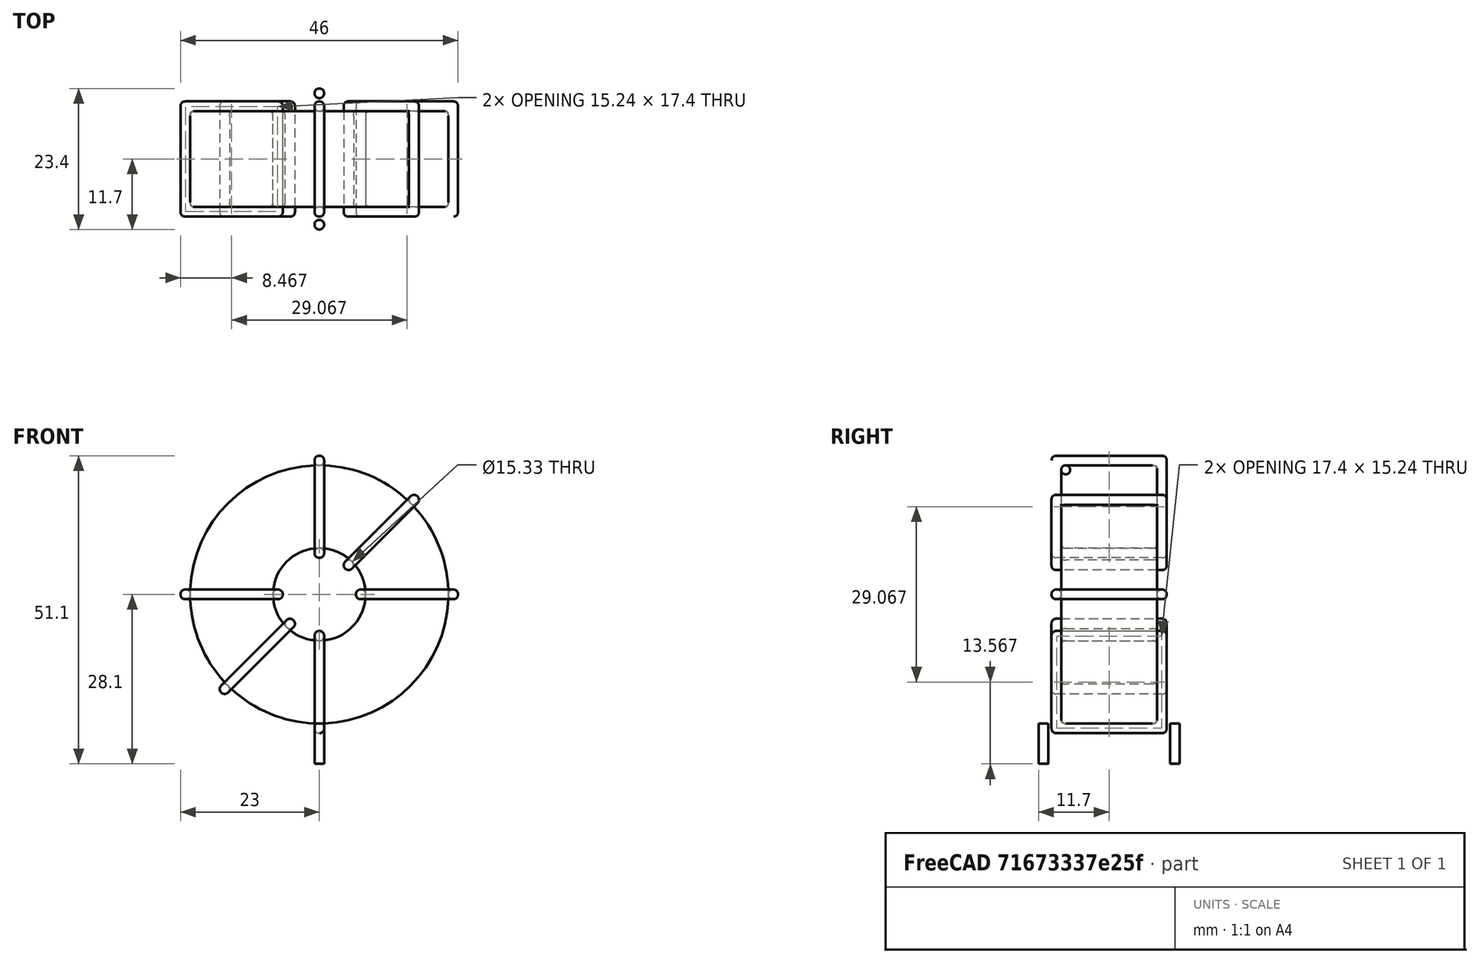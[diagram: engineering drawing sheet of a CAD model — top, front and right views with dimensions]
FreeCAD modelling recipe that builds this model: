
FCSTD DOCUMENT  (FreeCAD 0.16R6703 (Git))
Label: L_Toroid_Vertical_L46.0mm_W19.1mm_P21.80mm_Bourns_5700series
License: All rights reserved
LicenseURL: http://en.wikipedia.org/wiki/All_rights_reserved
objects: Sketcher::SketchObject×6, PartDesign::Pad×6, PartDesign::Fillet×5, Spreadsheet::Sheet×1
note: 23 computed .brp shape members not serialized (recipe doc carries the construction recipe); baked Part::Feature solids carry a one-line shape summary decoded from their .brp

FEATURE [Spreadsheet::Sheet] Spreadsheet  label="dimensions"
  cells = A1=Wx; B1(Wx)=46; C1(WW)=15.33333333333333; D1=46; A2=Wy; B2(Wy)=19.1; D2=19.1; A3=RM; B3(RMx)=21.8; C3(RMy)=0; A4=d_wire; B4(d_wire)=1.6; A5=H; B5(H)=46; A6=offsetx; B6(offsetx)=23
FEATURE [Sketcher::SketchObject] Sketch
  Placement = pos=(0,-10.9,0) rot=(1,0,0;1.5708rad)
  expr: Placement.Base.y = -Spreadsheet.RMx / 2
  expr: Constraints[0] = Spreadsheet.Wx / 2 - Spreadsheet.d_wire
  expr: Constraints[4] = Spreadsheet.WW / 2
  expr: Constraints[2] = Spreadsheet.Wx / 2 + Spreadsheet.d_wire + 0.5
  sketch-geometry (2):
    g0: Circle CenterX=0 CenterY=25.1 CenterZ=0 NormalX=0 NormalY=0 NormalZ=1 Radius=21.4
    g1: Circle CenterX=0 CenterY=25.1 CenterZ=0 NormalX=0 NormalY=0 NormalZ=1 Radius=7.66667
  constraints (5):
    c: Radius(g0) = 21.4
    c: DistanceX(g-1,g0) = 0
    c: DistanceY(g-1,g0) = 25.1
    c: Coincident(g1,g0)
    c: Radius(g1) = 7.66667
FEATURE [PartDesign::Pad] Pad
  Length = 15.9
  Length2 = 100
  Midplane = true
  Placement = pos=(0,-10.9,0) rot=(1,0,0;1.5708rad)
  Sketch = -> Sketch
  Type = 0
  expr: Length = Spreadsheet.Wy - 2 * Spreadsheet.d_wire
FEATURE [Sketcher::SketchObject] Sketch001
  Placement = pos=(0,0,2.1) rot=(0,0,1;0rad)
  expr: Placement.Base.z = 0.5 + Spreadsheet.d_wire
  expr: Constraints[4] = Spreadsheet.RMy
  expr: Constraints[2] = -Spreadsheet.RMx
  expr: Constraints[1] = Spreadsheet.d_wire / 2
  sketch-geometry (2):
    g0: Circle CenterX=0 CenterY=0 CenterZ=0 NormalX=0 NormalY=0 NormalZ=1 Radius=0.8
    g1: Circle CenterX=0 CenterY=-21.8 CenterZ=0 NormalX=0 NormalY=0 NormalZ=1 Radius=0.8
  constraints (5):
    c: Equal(g0,g1)
    c: Radius(g0) = 0.8
    c: DistanceY(g-1,g1) = -21.8
    c: Coincident(g0,g-1)
    c: DistanceX(g-1,g1) = 0
FEATURE [PartDesign::Pad] Pad001
  Length = 1.6
  Length2 = 5.1
  Placement = pos=(0,0,2.1) rot=(0,0,1;0rad)
  Reversed = true
  Sketch = -> Sketch001
  Type = 4
  expr: Length2 = 3.5 + Spreadsheet.d_wire
  expr: Length = Spreadsheet.d_wire
FEATURE [PartDesign::Fillet] Fillet
  Base = -> Pad [Edge6,Edge3,Edge2]
  Placement = pos=(0,-10.9,0) rot=(1,0,0;1.5708rad)
  Radius = 0.5
FEATURE [Sketcher::SketchObject] Sketch003
  Placement = pos=(0,-1.35,25.1) rot=(1,0,0;3.14159rad)
  expr: Constraints[18] = Spreadsheet.d_wire
  expr: Constraints[16] = Spreadsheet.d_wire
  expr: Constraints[19] = Spreadsheet.d_wire
  expr: Constraints[17] = Spreadsheet.d_wire
  expr: Placement.Base.y = -1 * (Spreadsheet.RMx - Spreadsheet.Wy) / 2
  expr: Constraints[21] = (Spreadsheet.Wx - Spreadsheet.WW) / 2 - Spreadsheet.d_wire
  expr: Constraints[22] = Spreadsheet.Wx / 2 - Spreadsheet.d_wire
  expr: Constraints[43] = Spreadsheet.d_wire
  expr: Constraints[48] = Spreadsheet.Wx - Spreadsheet.d_wire * 2
  expr: Constraints[49] = Spreadsheet.Wy
  expr: Placement.Base.z = Spreadsheet.Wx / 2 + Spreadsheet.d_wire + 0.5
  sketch-geometry (16):
    g0: LineSegment StartX=-6.06667 StartY=0 StartZ=0 EndX=-23 EndY=0 EndZ=0
    g1: LineSegment StartX=-23 StartY=0 StartZ=0 EndX=-23 EndY=19.1 EndZ=0
    g2: LineSegment StartX=-23 StartY=19.1 StartZ=0 EndX=-6.06667 EndY=19.1 EndZ=0
    g3: LineSegment StartX=-6.06667 StartY=19.1 StartZ=0 EndX=-6.06667 EndY=0 EndZ=0
    g4: LineSegment StartX=-21.4 StartY=17.5 StartZ=0 EndX=-7.66667 EndY=17.5 EndZ=0
    g5: LineSegment StartX=-7.66667 StartY=17.5 StartZ=0 EndX=-7.66667 EndY=1.6 EndZ=0
    g6: LineSegment StartX=-7.66667 StartY=1.6 StartZ=0 EndX=-21.4 EndY=1.6 EndZ=0
    g7: LineSegment StartX=-21.4 StartY=1.6 StartZ=0 EndX=-21.4 EndY=17.5 EndZ=0
    g8: LineSegment StartX=6.06667 StartY=19.1 StartZ=0 EndX=23 EndY=19.1 EndZ=0
    g9: LineSegment StartX=23 StartY=19.1 StartZ=0 EndX=23 EndY=0 EndZ=0
    g10: LineSegment StartX=23 StartY=0 StartZ=0 EndX=6.06667 EndY=0 EndZ=0
    g11: LineSegment StartX=6.06667 StartY=0 StartZ=0 EndX=6.06667 EndY=19.1 EndZ=0
    g12: LineSegment StartX=7.66667 StartY=17.5 StartZ=0 EndX=21.4 EndY=17.5 EndZ=0
    g13: LineSegment StartX=21.4 StartY=17.5 StartZ=0 EndX=21.4 EndY=1.6 EndZ=0
    g14: LineSegment StartX=21.4 StartY=1.6 StartZ=0 EndX=7.66667 EndY=1.6 EndZ=0
    g15: LineSegment StartX=7.66667 StartY=1.6 StartZ=0 EndX=7.66667 EndY=17.5 EndZ=0
  constraints (50):
    c: Horizontal(g0)
    c: Coincident(g1,g0)
    c: Vertical(g1)
    c: Coincident(g2,g1)
    c: Horizontal(g2)
    c: Coincident(g3,g2)
    c: Coincident(g3,g0)
    c: Vertical(g3)
    c: Coincident(g4,g5)
    c: Coincident(g5,g6)
    c: Coincident(g6,g7)
    c: Coincident(g7,g4)
    c: Horizontal(g4)
    c: Horizontal(g6)
    c: Vertical(g5)
    c: Vertical(g7)
    c: DistanceX(g1,g4) = 1.6
    c: DistanceY(g4,g1) = 1.6
    c: DistanceX(g5,g0) = 1.6
    c: DistanceY(g0,g5) = 1.6
    c: DistanceY(g-1,g0) = 0
    c: DistanceX(g6,g6) = 13.7333
    c: DistanceX(g6,g-1) = 21.4
    c: Coincident(g8,g9)
    c: Coincident(g9,g10)
    c: Coincident(g10,g11)
    c: Coincident(g11,g8)
    c: Horizontal(g8)
    c: Horizontal(g10)
    c: Vertical(g9)
    c: Vertical(g11)
    c: Coincident(g12,g13)
    c: Coincident(g13,g14)
    c: Coincident(g14,g15)
    c: Coincident(g15,g12)
    c: Horizontal(g12)
    c: Horizontal(g14)
    c: Vertical(g13)
    c: Vertical(g15)
    c: DistanceY(g8,g2) = 0
    c: DistanceY(g10,g0) = 0
    c: DistanceY(g14,g5) = 0
    c: DistanceY(g12,g4) = 0
    c: DistanceX(g8,g12) = 1.6
    c: Equal(g8,g2)
    c: Equal(g12,g4)
    c: Equal(g9,g1)
    c: Equal(g13,g7)
    c: DistanceX(g4,g12) = 42.8
    c: DistanceY(g0,g1) = 19.1
FEATURE [PartDesign::Pad] Pad002
  Length = 1.6
  Length2 = 100
  Midplane = true
  Placement = pos=(0,-1.35,25.1) rot=(1,0,0;3.14159rad)
  Sketch = -> Sketch003
  Type = 0
  expr: Length = Spreadsheet.d_wire
FEATURE [PartDesign::Fillet] Fillet001
  Base = -> Pad002 [Edge38,Edge41,Edge42,Edge43,Edge29,Edge32,Edge33,Edge34,Edge25,Edge35,Edge36,Edge13,Edge14,Edge15,Edge16,Edge17,Edge18,Edge19,Edge1,Edge2,Edge3,Edge4,Edge5,Edge6,Edge7,Edge37,Edge39,Edge40,Edge20,Edge23,Edge24,Edge21,Edge22,Edge8,Edge9,Edge10,Edge11,Edge12,Edge26,Edge27,+8 more]
  Placement = pos=(0,-1.35,25.1) rot=(1,0,0;3.14159rad)
  Radius = 0.752
  expr: Radius = Spreadsheet.d_wire * 0.47
FEATURE [Sketcher::SketchObject] Sketch004
  Placement = pos=(0,-1.35,25.1) rot=(0.92388,0,0.382683;3.14159rad)
  expr: Constraints[18] = Spreadsheet.d_wire
  expr: Constraints[16] = Spreadsheet.d_wire
  expr: Constraints[19] = Spreadsheet.d_wire
  expr: Constraints[17] = Spreadsheet.d_wire
  expr: Placement.Base.y = -1 * (Spreadsheet.RMx - Spreadsheet.Wy) / 2
  expr: Constraints[21] = (Spreadsheet.Wx - Spreadsheet.WW) / 2 - Spreadsheet.d_wire
  expr: Constraints[22] = Spreadsheet.Wx / 2 - Spreadsheet.d_wire
  expr: Constraints[43] = Spreadsheet.d_wire
  expr: Constraints[48] = Spreadsheet.Wx - 2 * Spreadsheet.d_wire
  expr: Constraints[49] = Spreadsheet.Wy
  expr: Placement.Base.z = Spreadsheet.Wx / 2 + Spreadsheet.d_wire + 0.5
  sketch-geometry (16):
    g0: LineSegment StartX=-6.06667 StartY=0 StartZ=0 EndX=-23 EndY=0 EndZ=0
    g1: LineSegment StartX=-23 StartY=0 StartZ=0 EndX=-23 EndY=19.1 EndZ=0
    g2: LineSegment StartX=-23 StartY=19.1 StartZ=0 EndX=-6.06667 EndY=19.1 EndZ=0
    g3: LineSegment StartX=-6.06667 StartY=19.1 StartZ=0 EndX=-6.06667 EndY=0 EndZ=0
    g4: LineSegment StartX=-21.4 StartY=17.5 StartZ=0 EndX=-7.66667 EndY=17.5 EndZ=0
    g5: LineSegment StartX=-7.66667 StartY=17.5 StartZ=0 EndX=-7.66667 EndY=1.6 EndZ=0
    g6: LineSegment StartX=-7.66667 StartY=1.6 StartZ=0 EndX=-21.4 EndY=1.6 EndZ=0
    g7: LineSegment StartX=-21.4 StartY=1.6 StartZ=0 EndX=-21.4 EndY=17.5 EndZ=0
    g8: LineSegment StartX=6.06667 StartY=19.1 StartZ=0 EndX=23 EndY=19.1 EndZ=0
    g9: LineSegment StartX=23 StartY=19.1 StartZ=0 EndX=23 EndY=0 EndZ=0
    g10: LineSegment StartX=23 StartY=0 StartZ=0 EndX=6.06667 EndY=0 EndZ=0
    g11: LineSegment StartX=6.06667 StartY=0 StartZ=0 EndX=6.06667 EndY=19.1 EndZ=0
    g12: LineSegment StartX=7.66667 StartY=17.5 StartZ=0 EndX=21.4 EndY=17.5 EndZ=0
    g13: LineSegment StartX=21.4 StartY=17.5 StartZ=0 EndX=21.4 EndY=1.6 EndZ=0
    g14: LineSegment StartX=21.4 StartY=1.6 StartZ=0 EndX=7.66667 EndY=1.6 EndZ=0
    g15: LineSegment StartX=7.66667 StartY=1.6 StartZ=0 EndX=7.66667 EndY=17.5 EndZ=0
  constraints (50):
    c: Horizontal(g0)
    c: Coincident(g1,g0)
    c: Vertical(g1)
    c: Coincident(g2,g1)
    c: Horizontal(g2)
    c: Coincident(g3,g2)
    c: Coincident(g3,g0)
    c: Vertical(g3)
    c: Coincident(g4,g5)
    c: Coincident(g5,g6)
    c: Coincident(g6,g7)
    c: Coincident(g7,g4)
    c: Horizontal(g4)
    c: Horizontal(g6)
    c: Vertical(g5)
    c: Vertical(g7)
    c: DistanceX(g1,g4) = 1.6
    c: DistanceY(g4,g1) = 1.6
    c: DistanceX(g5,g0) = 1.6
    c: DistanceY(g0,g5) = 1.6
    c: DistanceY(g-1,g0) = 0
    c: DistanceX(g6,g6) = 13.7333
    c: DistanceX(g6,g-1) = 21.4
    c: Coincident(g8,g9)
    c: Coincident(g9,g10)
    c: Coincident(g10,g11)
    c: Coincident(g11,g8)
    c: Horizontal(g8)
    c: Horizontal(g10)
    c: Vertical(g9)
    c: Vertical(g11)
    c: Coincident(g12,g13)
    c: Coincident(g13,g14)
    c: Coincident(g14,g15)
    c: Coincident(g15,g12)
    c: Horizontal(g12)
    c: Horizontal(g14)
    c: Vertical(g13)
    c: Vertical(g15)
    c: DistanceY(g8,g2) = 0
    c: DistanceY(g10,g0) = 0
    c: DistanceY(g14,g5) = 0
    c: DistanceY(g12,g4) = 0
    c: DistanceX(g8,g12) = 1.6
    c: Equal(g8,g2)
    c: Equal(g12,g4)
    c: Equal(g9,g1)
    c: Equal(g13,g7)
    c: DistanceX(g4,g12) = 42.8
    c: DistanceY(g0,g1) = 19.1
FEATURE [PartDesign::Pad] Pad003
  Length = 1.6
  Length2 = 100
  Midplane = true
  Placement = pos=(0,-1.35,25.1) rot=(0.92388,0,0.382683;3.14159rad)
  Sketch = -> Sketch004
  Type = 0
  expr: Length = Spreadsheet.d_wire
FEATURE [PartDesign::Fillet] Fillet002
  Base = -> Pad003 [Edge38,Edge41,Edge42,Edge43,Edge29,Edge32,Edge33,Edge34,Edge25,Edge35,Edge36,Edge13,Edge14,Edge15,Edge16,Edge17,Edge18,Edge19,Edge1,Edge2,Edge3,Edge4,Edge5,Edge6,Edge7,Edge37,Edge39,Edge40,Edge20,Edge23,Edge24,Edge21,Edge22,Edge8,Edge9,Edge10,Edge11,Edge12,Edge26,Edge27,+8 more]
  Placement = pos=(0,-1.35,25.1) rot=(0.92388,0,0.382683;3.14159rad)
  Radius = 0.752
  expr: Radius = Spreadsheet.d_wire * 0.47
FEATURE [Sketcher::SketchObject] Sketch005
  Placement = pos=(0,-1.35,25.1) rot=(0.92388,0,-0.382683;3.14159rad)
  expr: Constraints[18] = Spreadsheet.d_wire
  expr: Constraints[16] = Spreadsheet.d_wire
  expr: Constraints[19] = Spreadsheet.d_wire
  expr: Constraints[17] = Spreadsheet.d_wire
  expr: Placement.Base.y = -1 * (Spreadsheet.RMx - Spreadsheet.Wy) / 2
  expr: Constraints[21] = (Spreadsheet.Wx - Spreadsheet.WW) / 2 - Spreadsheet.d_wire
  expr: Constraints[22] = Spreadsheet.Wx / 2 - Spreadsheet.d_wire
  expr: Constraints[43] = Spreadsheet.d_wire
  expr: Constraints[48] = Spreadsheet.Wx - 2 * Spreadsheet.d_wire
  expr: Constraints[49] = Spreadsheet.Wy
  expr: Placement.Base.z = Spreadsheet.Wx / 2 + Spreadsheet.d_wire + 0.5
  sketch-geometry (16):
    g0: LineSegment StartX=-6.06667 StartY=0 StartZ=0 EndX=-23 EndY=0 EndZ=0
    g1: LineSegment StartX=-23 StartY=0 StartZ=0 EndX=-23 EndY=19.1 EndZ=0
    g2: LineSegment StartX=-23 StartY=19.1 StartZ=0 EndX=-6.06667 EndY=19.1 EndZ=0
    g3: LineSegment StartX=-6.06667 StartY=19.1 StartZ=0 EndX=-6.06667 EndY=0 EndZ=0
    g4: LineSegment StartX=-21.4 StartY=17.5 StartZ=0 EndX=-7.66667 EndY=17.5 EndZ=0
    g5: LineSegment StartX=-7.66667 StartY=17.5 StartZ=0 EndX=-7.66667 EndY=1.6 EndZ=0
    g6: LineSegment StartX=-7.66667 StartY=1.6 StartZ=0 EndX=-21.4 EndY=1.6 EndZ=0
    g7: LineSegment StartX=-21.4 StartY=1.6 StartZ=0 EndX=-21.4 EndY=17.5 EndZ=0
    g8: LineSegment StartX=6.06667 StartY=19.1 StartZ=0 EndX=23 EndY=19.1 EndZ=0
    g9: LineSegment StartX=23 StartY=19.1 StartZ=0 EndX=23 EndY=0 EndZ=0
    g10: LineSegment StartX=23 StartY=0 StartZ=0 EndX=6.06667 EndY=0 EndZ=0
    g11: LineSegment StartX=6.06667 StartY=0 StartZ=0 EndX=6.06667 EndY=19.1 EndZ=0
    g12: LineSegment StartX=7.66667 StartY=17.5 StartZ=0 EndX=21.4 EndY=17.5 EndZ=0
    g13: LineSegment StartX=21.4 StartY=17.5 StartZ=0 EndX=21.4 EndY=1.6 EndZ=0
    g14: LineSegment StartX=21.4 StartY=1.6 StartZ=0 EndX=7.66667 EndY=1.6 EndZ=0
    g15: LineSegment StartX=7.66667 StartY=1.6 StartZ=0 EndX=7.66667 EndY=17.5 EndZ=0
  constraints (50):
    c: Horizontal(g0)
    c: Coincident(g1,g0)
    c: Vertical(g1)
    c: Coincident(g2,g1)
    c: Horizontal(g2)
    c: Coincident(g3,g2)
    c: Coincident(g3,g0)
    c: Vertical(g3)
    c: Coincident(g4,g5)
    c: Coincident(g5,g6)
    c: Coincident(g6,g7)
    c: Coincident(g7,g4)
    c: Horizontal(g4)
    c: Horizontal(g6)
    c: Vertical(g5)
    c: Vertical(g7)
    c: DistanceX(g1,g4) = 1.6
    c: DistanceY(g4,g1) = 1.6
    c: DistanceX(g5,g0) = 1.6
    c: DistanceY(g0,g5) = 1.6
    c: DistanceY(g-1,g0) = 0
    c: DistanceX(g6,g6) = 13.7333
    c: DistanceX(g6,g-1) = 21.4
    c: Coincident(g8,g9)
    c: Coincident(g9,g10)
    c: Coincident(g10,g11)
    c: Coincident(g11,g8)
    c: Horizontal(g8)
    c: Horizontal(g10)
    c: Vertical(g9)
    c: Vertical(g11)
    c: Coincident(g12,g13)
    c: Coincident(g13,g14)
    c: Coincident(g14,g15)
    c: Coincident(g15,g12)
    c: Horizontal(g12)
    c: Horizontal(g14)
    c: Vertical(g13)
    c: Vertical(g15)
    c: DistanceY(g8,g2) = 0
    c: DistanceY(g10,g0) = 0
    c: DistanceY(g14,g5) = 0
    c: DistanceY(g12,g4) = 0
    c: DistanceX(g8,g12) = 1.6
    c: Equal(g8,g2)
    c: Equal(g12,g4)
    c: Equal(g9,g1)
    c: Equal(g13,g7)
    c: DistanceX(g4,g12) = 42.8
    c: DistanceY(g0,g1) = 19.1
FEATURE [PartDesign::Pad] Pad004
  Length = 1.6
  Length2 = 100
  Midplane = true
  Placement = pos=(0,-1.35,25.1) rot=(0.92388,0,-0.382683;3.14159rad)
  Sketch = -> Sketch005
  Type = 0
  expr: Length = Spreadsheet.d_wire
FEATURE [PartDesign::Fillet] Fillet003
  Base = -> Pad004 [Edge38,Edge41,Edge42,Edge43,Edge29,Edge32,Edge33,Edge34,Edge25,Edge35,Edge36,Edge13,Edge14,Edge15,Edge16,Edge17,Edge18,Edge19,Edge1,Edge2,Edge3,Edge4,Edge5,Edge6,Edge7,Edge37,Edge39,Edge40,Edge20,Edge23,Edge24,Edge21,Edge22,Edge8,Edge9,Edge10,Edge11,Edge12,Edge26,Edge27,+8 more]
  Placement = pos=(0,-1.35,25.1) rot=(0.92388,0,-0.382683;3.14159rad)
  Radius = 0.752
  expr: Radius = Spreadsheet.d_wire * 0.47
FEATURE [Sketcher::SketchObject] Sketch006
  Placement = pos=(0,-1.35,25.1) rot=(0.707107,0,0.707107;3.14159rad)
  expr: Constraints[18] = Spreadsheet.d_wire
  expr: Constraints[16] = Spreadsheet.d_wire
  expr: Constraints[19] = Spreadsheet.d_wire
  expr: Constraints[17] = Spreadsheet.d_wire
  expr: Placement.Base.y = -1 * (Spreadsheet.RMx - Spreadsheet.Wy) / 2
  expr: Constraints[21] = (Spreadsheet.Wx - Spreadsheet.WW) / 2 - Spreadsheet.d_wire
  expr: Constraints[22] = Spreadsheet.Wx / 2 - Spreadsheet.d_wire
  expr: Constraints[43] = Spreadsheet.d_wire
  expr: Constraints[48] = Spreadsheet.Wx - Spreadsheet.d_wire * 2
  expr: Constraints[49] = Spreadsheet.Wy
  expr: Placement.Base.z = Spreadsheet.Wx / 2 + Spreadsheet.d_wire + 0.5
  sketch-geometry (16):
    g0: LineSegment StartX=-6.06667 StartY=0 StartZ=0 EndX=-23 EndY=0 EndZ=0
    g1: LineSegment StartX=-23 StartY=0 StartZ=0 EndX=-23 EndY=19.1 EndZ=0
    g2: LineSegment StartX=-23 StartY=19.1 StartZ=0 EndX=-6.06667 EndY=19.1 EndZ=0
    g3: LineSegment StartX=-6.06667 StartY=19.1 StartZ=0 EndX=-6.06667 EndY=0 EndZ=0
    g4: LineSegment StartX=-21.4 StartY=17.5 StartZ=0 EndX=-7.66667 EndY=17.5 EndZ=0
    g5: LineSegment StartX=-7.66667 StartY=17.5 StartZ=0 EndX=-7.66667 EndY=1.6 EndZ=0
    g6: LineSegment StartX=-7.66667 StartY=1.6 StartZ=0 EndX=-21.4 EndY=1.6 EndZ=0
    g7: LineSegment StartX=-21.4 StartY=1.6 StartZ=0 EndX=-21.4 EndY=17.5 EndZ=0
    g8: LineSegment StartX=6.06667 StartY=19.1 StartZ=0 EndX=23 EndY=19.1 EndZ=0
    g9: LineSegment StartX=23 StartY=19.1 StartZ=0 EndX=23 EndY=0 EndZ=0
    g10: LineSegment StartX=23 StartY=0 StartZ=0 EndX=6.06667 EndY=0 EndZ=0
    g11: LineSegment StartX=6.06667 StartY=0 StartZ=0 EndX=6.06667 EndY=19.1 EndZ=0
    g12: LineSegment StartX=7.66667 StartY=17.5 StartZ=0 EndX=21.4 EndY=17.5 EndZ=0
    g13: LineSegment StartX=21.4 StartY=17.5 StartZ=0 EndX=21.4 EndY=1.6 EndZ=0
    g14: LineSegment StartX=21.4 StartY=1.6 StartZ=0 EndX=7.66667 EndY=1.6 EndZ=0
    g15: LineSegment StartX=7.66667 StartY=1.6 StartZ=0 EndX=7.66667 EndY=17.5 EndZ=0
  constraints (50):
    c: Horizontal(g0)
    c: Coincident(g1,g0)
    c: Vertical(g1)
    c: Coincident(g2,g1)
    c: Horizontal(g2)
    c: Coincident(g3,g2)
    c: Coincident(g3,g0)
    c: Vertical(g3)
    c: Coincident(g4,g5)
    c: Coincident(g5,g6)
    c: Coincident(g6,g7)
    c: Coincident(g7,g4)
    c: Horizontal(g4)
    c: Horizontal(g6)
    c: Vertical(g5)
    c: Vertical(g7)
    c: DistanceX(g1,g4) = 1.6
    c: DistanceY(g4,g1) = 1.6
    c: DistanceX(g5,g0) = 1.6
    c: DistanceY(g0,g5) = 1.6
    c: DistanceY(g-1,g0) = 0
    c: DistanceX(g6,g6) = 13.7333
    c: DistanceX(g6,g-1) = 21.4
    c: Coincident(g8,g9)
    c: Coincident(g9,g10)
    c: Coincident(g10,g11)
    c: Coincident(g11,g8)
    c: Horizontal(g8)
    c: Horizontal(g10)
    c: Vertical(g9)
    c: Vertical(g11)
    c: Coincident(g12,g13)
    c: Coincident(g13,g14)
    c: Coincident(g14,g15)
    c: Coincident(g15,g12)
    c: Horizontal(g12)
    c: Horizontal(g14)
    c: Vertical(g13)
    c: Vertical(g15)
    c: DistanceY(g8,g2) = 0
    c: DistanceY(g10,g0) = 0
    c: DistanceY(g14,g5) = 0
    c: DistanceY(g12,g4) = 0
    c: DistanceX(g8,g12) = 1.6
    c: Equal(g8,g2)
    c: Equal(g12,g4)
    c: Equal(g9,g1)
    c: Equal(g13,g7)
    c: DistanceX(g4,g12) = 42.8
    c: DistanceY(g0,g1) = 19.1
FEATURE [PartDesign::Pad] Pad005
  Length = 1.6
  Length2 = 100
  Midplane = true
  Placement = pos=(0,-1.35,25.1) rot=(0.707107,0,0.707107;3.14159rad)
  Sketch = -> Sketch006
  Type = 0
  expr: Length = Spreadsheet.d_wire
FEATURE [PartDesign::Fillet] Fillet004
  Base = -> Pad005 [Edge38,Edge41,Edge42,Edge43,Edge29,Edge32,Edge33,Edge34,Edge25,Edge35,Edge36,Edge13,Edge14,Edge15,Edge16,Edge17,Edge18,Edge19,Edge1,Edge2,Edge3,Edge4,Edge5,Edge6,Edge7,Edge37,Edge39,Edge40,Edge20,Edge23,Edge24,Edge21,Edge22,Edge8,Edge9,Edge10,Edge11,Edge12,Edge26,Edge27,+8 more]
  Placement = pos=(0,-1.35,25.1) rot=(0.707107,0,0.707107;3.14159rad)
  Radius = 0.752
  expr: Radius = Spreadsheet.d_wire * 0.47
